# Revit family: SINGLE OUTSWINGING TERRACE DOOR WITH TRANSOM WITHOUT KICKPLATE_Arc
name_source: partatom
category: Doors
revit_build: Autodesk Revit 2017 (Build: 20160225_1515(x64)
units: mm (PartAtom-declared; Revit-internal decimal feet)

## family parameters
Always vertical = Yes
Cut with Voids When Loaded = No
Host = Wall
OmniClass Number = 23.30.10.00
OmniClass Title = Doors
Room Calculation Point = No
Shared = No

## types (1)
- SINGLE OUTSWINGING TERRACE DOOR WITH TRANSOM WITHOUT KICKPLATE_Arc
    Analytic Construction = <None>
    Assembly Code = B2030
    Description = TERRASWING ACCESS-SINGLE OUTSWINGING TERRACE DOOR WITH TRANSOM WITHOUT KICKPLATE
    Frame Material = Aluminum
    Function = Interior
    Glass Material = Glass
    Height = 11' - 0"
    Keynote = 08 11 00
    Manufacturer = Oldcastle BuildingEnvelope®
    Model = TS-AS
    Operable Height = 8' - 0"
    Rough Height = 11' - 0 1/4"
    Rough Width = 4' - 0 1/2"
    Transom Height = 3' - 0"
    URL = obe.com
    Wall Closure = By host
    Width = 4' - 0"

## geometry (parser evidence)
native form markers: Blend x2, Sweep x2
no freeform markers — native parametric forms only
